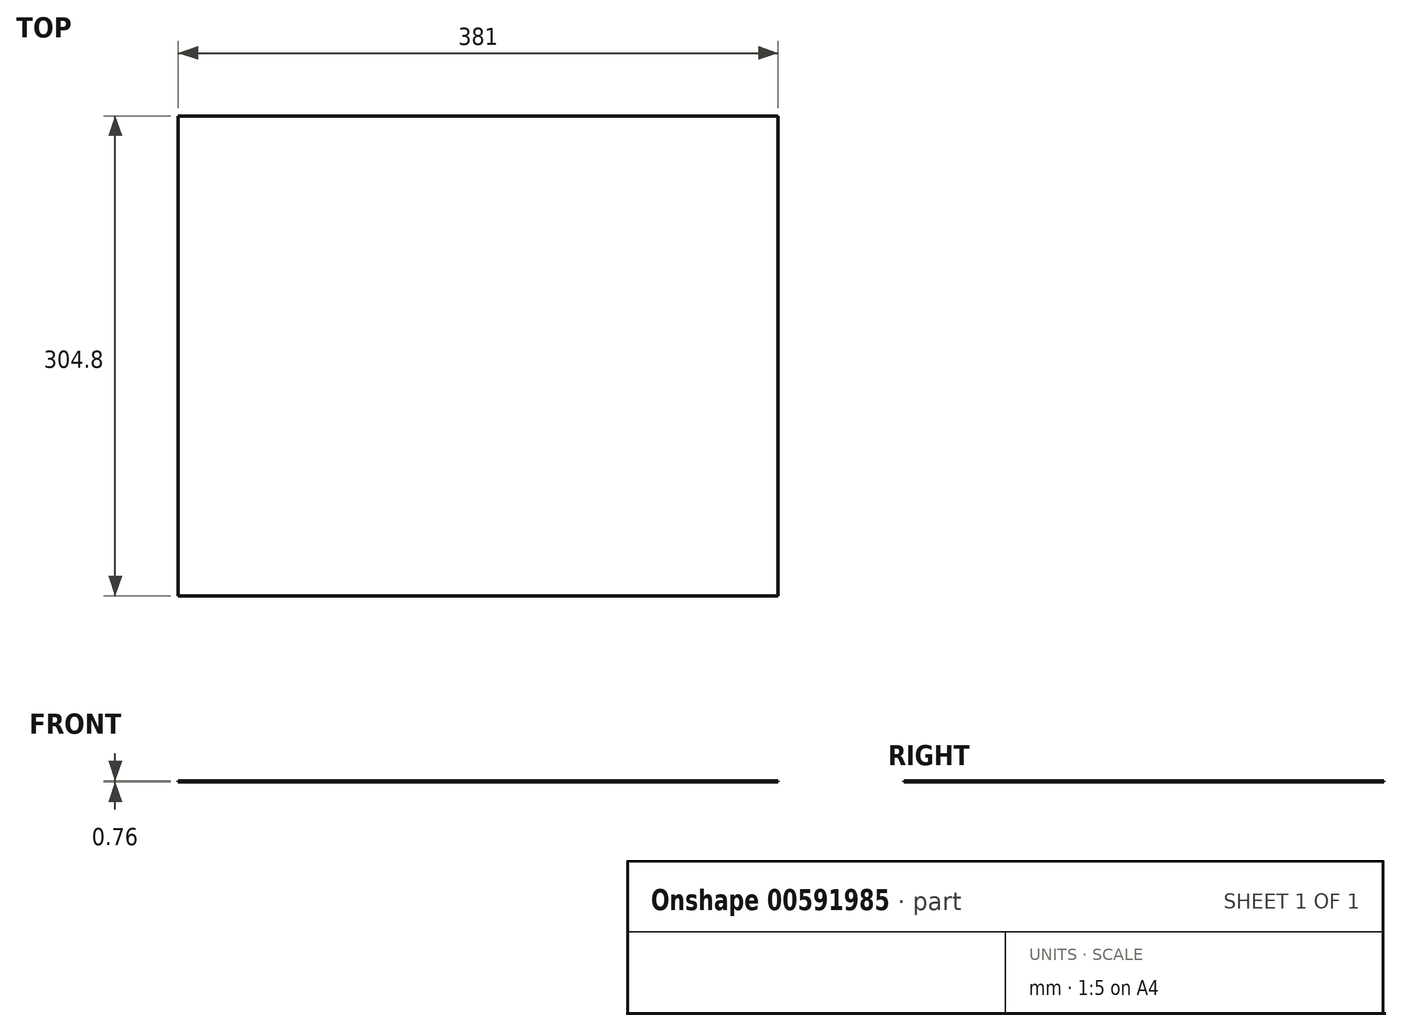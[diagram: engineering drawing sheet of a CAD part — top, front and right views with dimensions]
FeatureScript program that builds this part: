
annotation { "Feature Type Name" : "Feature", "Feature Type Description" : "" }
export const myFeature = defineFeature(function(context is Context, id is Id, definition is map)
    precondition{}
    {
        {
            var Q0;
            Q0=qCreatedBy(makeId("Top.planeOp"),FACE);
            var sketch = newSketch(context, id + "F0", { "sketchPlane" : qUnion([Q0])});
            skLineSegment(sketch, "E0.bottom", {"start": v(0, 304.8) * mm, "end": v(381, 304.8) * mm});
            skLineSegment(sketch, "E0.top", {"start": v(0, 0) * mm, "end": v(381, 0) * mm});
            skLineSegment(sketch, "E0.left", {"start": v(0, 304.8) * mm, "end": v(0, 0) * mm});
            skLineSegment(sketch, "E0.right", {"start": v(381, 304.8) * mm, "end": v(381, 0) * mm});
            skLineSegment(sketch, "E1", {"start": v(127, 0) * mm, "end": v(127, 304.8) * mm, "construction": true});
            skLineSegment(sketch, "E2", {"start": v(254, 0) * mm, "end": v(254, 304.8) * mm, "construction": true});
            skSolve(sketch);
        }
        {
            var Q0;
            Q0=makeQuery(id+"F0.imprint","IMPRINT",FACE,{"disambiguationData":[TD([[makeQuery(id+"F0.imprint","IMPRINT",EDGE,{"derivedFrom":sQuery(id+"F0.wireOp",EDGE,"E0.bottom")}),-1.0]])]});
            extrude(context, id + "F1", {"entities" : qUnion([Q0]), "depth" : 0.76 * mm, "offsetDistance" : 25.4 * mm});
        }
    });
